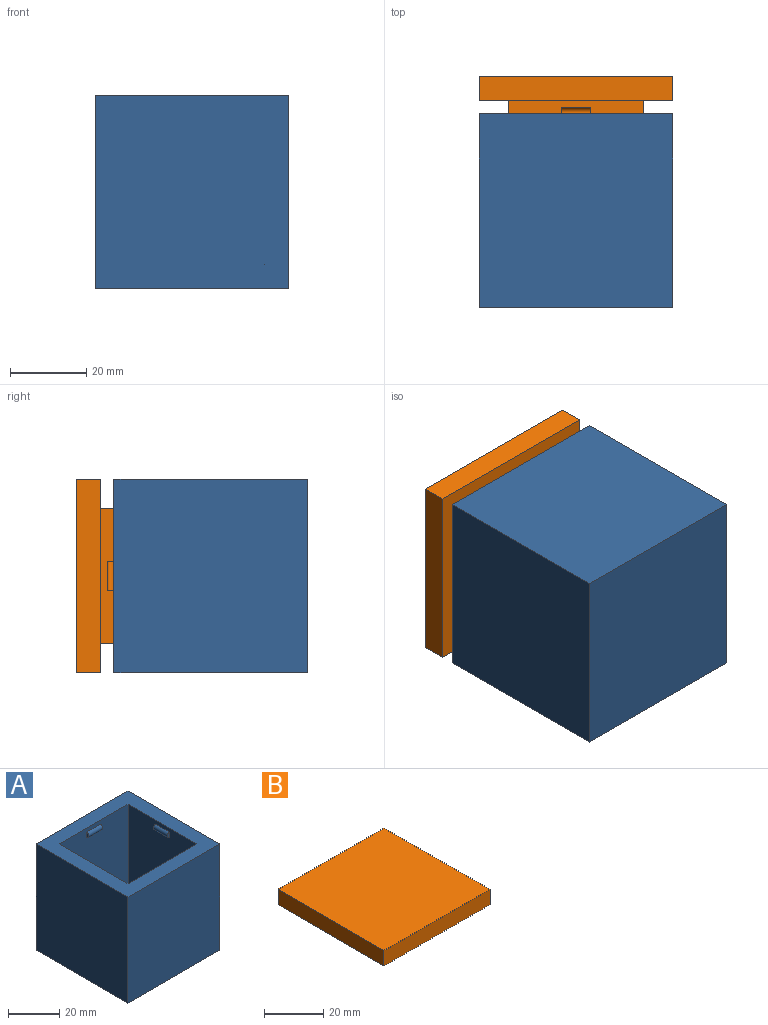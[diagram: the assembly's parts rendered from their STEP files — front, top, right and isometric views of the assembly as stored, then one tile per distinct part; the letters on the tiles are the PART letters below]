
ASSEMBLY  parts=2 mates=1
PART A: 23 faces, bbox 50.8x50.8x50.8 mm
  f0: plane 44.45x38.1mm, normal (0,-1,0), area 1674.2mm2, adj f1,f7,f9,f10,f11,f12,f13
  f1: plane 50.8x50.8mm, normal (0,0,1), area 1129mm2, adj f0,f2,f3,f4,f5,f7,f8,f9
  f2: plane 50.8x50.8mm, normal (0,1,0), area 2580.6mm2, adj f1,f3,f5,f6
  f3: plane 50.8x50.8mm, normal (-1,0,0), area 2580.6mm2, adj f1,f2,f4,f6
  f4: plane 50.8x50.8mm, normal (0,-1,0), area 2580.6mm2, adj f1,f3,f5,f6
  f5: plane 50.8x50.8mm, normal (1,0,0), area 2580.6mm2, adj f1,f2,f4,f6
  f6: plane 50.8x50.8mm, normal (0,0,-1), area 2580.6mm2, adj f2,f3,f4,f5
  f7: plane 44.45x38.1mm, normal (1,0,0), area 1674.2mm2, adj f0,f1,f8,f10,f14,f15,f16
  f8: plane 44.45x38.1mm, normal (0,1,0), area 1674.2mm2, adj f1,f7,f9,f10,f17,f18,f19
  f9: plane 44.45x38.1mm, normal (-1,0,0), area 1674.2mm2, adj f0,f1,f8,f10,f20,f21,f22
  f10: plane 38.1x38.1mm, normal (0,0,1), area 1451.6mm2, adj f0,f7,f8,f9
  f11: plane 2.54x1.27mm, normal (-1,0,0), area 2.5mm2, adj f0,f12
  f12: cylinder r=1.27mm len=7.62mm, axis (-1,0,0), area 30.4mm2, adj f0,f11,f13
  f13: plane 2.54x1.27mm, normal (1,0,0), area 2.5mm2, adj f0,f12
  f14: plane 2.54x1.27mm, normal (0,-1,0), area 2.5mm2, adj f7,f16
  f15: plane 2.54x1.27mm, normal (0,1,0), area 2.5mm2, adj f7,f16
  f16: cylinder r=1.27mm len=7.62mm, axis (0,-1,0), area 30.4mm2, adj f7,f14,f15
  f17: plane 2.54x1.27mm, normal (1,0,0), area 2.5mm2, adj f8,f19
  f18: plane 2.54x1.27mm, normal (-1,0,0), area 2.5mm2, adj f8,f19
  f19: cylinder r=1.27mm len=7.62mm, axis (1,0,0), area 30.4mm2, adj f8,f17,f18
  f20: plane 2.54x1.27mm, normal (0,1,0), area 2.5mm2, adj f9,f22
  f21: plane 2.54x1.27mm, normal (0,-1,0), area 2.5mm2, adj f9,f22
  f22: cylinder r=1.27mm len=7.62mm, axis (0,1,0), area 30.4mm2, adj f9,f20,f21
PART B: 23 faces, bbox 50.8x50.8x12.7 mm
  f0: plane 35.56x6.35mm, normal (-1,0,0), area 206.5mm2, adj f1,f8,f9,f10,f20,f21,f22
  f1: plane 35.56x6.35mm, normal (0,1,0), area 206.5mm2, adj f0,f2,f9,f10,f17,f18,f19
  f2: plane 35.56x6.35mm, normal (1,0,0), area 206.5mm2, adj f1,f8,f9,f10,f14,f15,f16
  f3: plane 50.8x6.35mm, normal (0,1,0), area 322.6mm2, adj f4,f6,f7,f9
  f4: plane 50.8x6.35mm, normal (-1,0,0), area 322.6mm2, adj f3,f5,f7,f9
  f5: plane 50.8x6.35mm, normal (0,-1,0), area 322.6mm2, adj f4,f6,f7,f9
  f6: plane 50.8x6.35mm, normal (1,0,0), area 322.6mm2, adj f3,f5,f7,f9
  f7: plane 50.8x50.8mm, normal (0,0,1), area 2580.6mm2, adj f3,f4,f5,f6
  f8: plane 35.56x6.35mm, normal (0,-1,0), area 206.5mm2, adj f0,f2,f9,f10,f11,f12,f13
  f9: plane 50.8x50.8mm, normal (0,0,-1), area 1316.1mm2, adj f0,f1,f2,f3,f4,f5,f6,f8
  f10: plane 35.56x35.56mm, normal (0,0,-1), area 1264.5mm2, adj f0,f1,f2,f8
  f11: plane 2.54x1.27mm, normal (1,0,0), area 2.5mm2, adj f8,f13
  f12: plane 2.54x1.27mm, normal (-1,0,0), area 2.5mm2, adj f8,f13
  f13: cylinder r=1.27mm len=7.62mm, axis (1,0,0), area 30.4mm2, adj f8,f11,f12
  f14: plane 2.54x1.27mm, normal (0,1,0), area 2.5mm2, adj f2,f16
  f15: plane 2.54x1.27mm, normal (0,-1,0), area 2.5mm2, adj f2,f16
  f16: cylinder r=1.27mm len=7.62mm, axis (0,1,0), area 30.4mm2, adj f2,f14,f15
  f17: plane 2.54x1.27mm, normal (-1,0,0), area 2.5mm2, adj f1,f19
  f18: plane 2.54x1.27mm, normal (1,0,0), area 2.5mm2, adj f1,f19
  f19: cylinder r=1.27mm len=7.62mm, axis (-1,0,0), area 30.4mm2, adj f1,f17,f18
  f20: plane 2.54x1.27mm, normal (0,-1,0), area 2.5mm2, adj f0,f22
  f21: plane 2.54x1.27mm, normal (0,1,0), area 2.5mm2, adj f0,f22
  f22: cylinder r=1.27mm len=7.62mm, axis (0,-1,0), area 30.4mm2, adj f0,f20,f21
PLACE A rot(axis=(-1,0,0),90deg) t=(-18.07,-58.42,28.83)mm
PLACE B rot(axis=(-1,0,0),90deg) t=(-18.07,-10.41,28.83)mm
MATE parallel B.f9 <-> A.f1  axis (0,-1,0) through (-18.07,-4.06,28.83)mm
